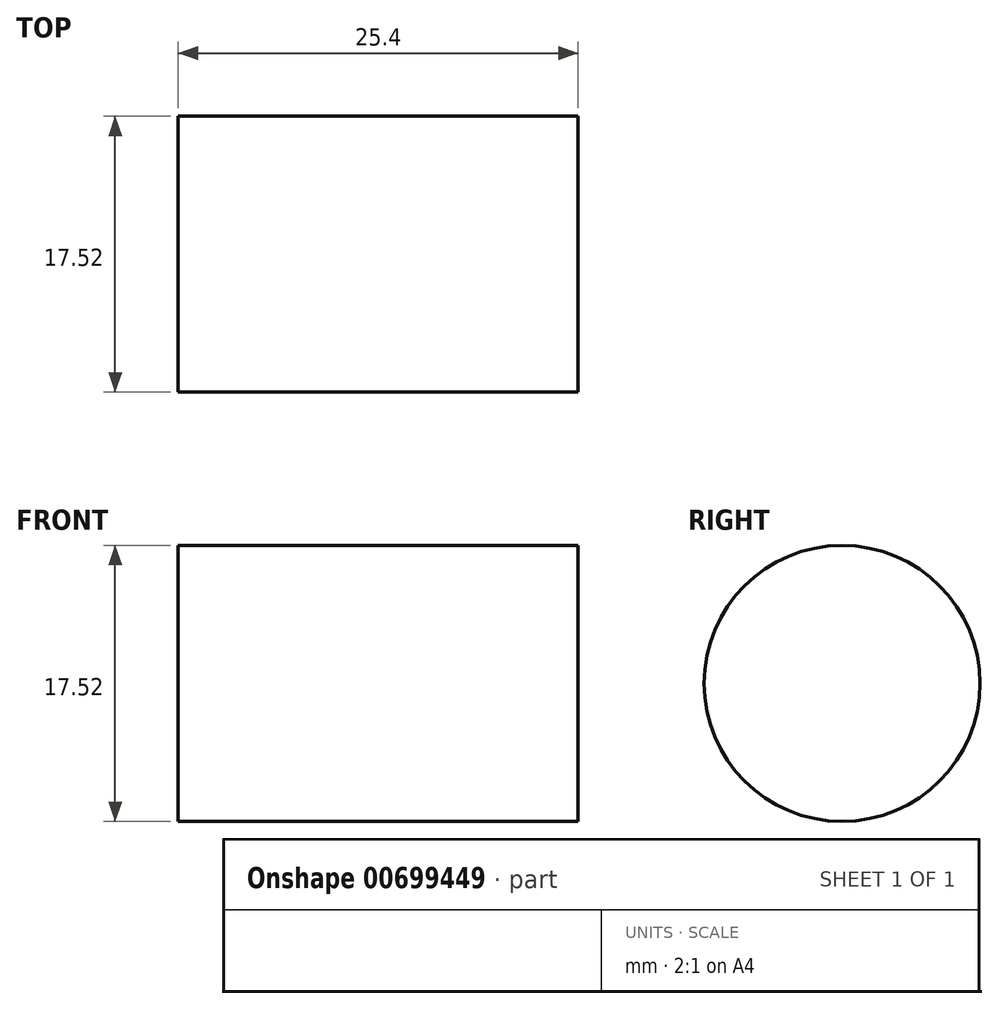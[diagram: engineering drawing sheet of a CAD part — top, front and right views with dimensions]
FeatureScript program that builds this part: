
annotation { "Feature Type Name" : "Feature", "Feature Type Description" : "" }
export const myFeature = defineFeature(function(context is Context, id is Id, definition is map)
    precondition{}
    {
        {
            var Q0;
            Q0=qCreatedBy(makeId("Right.planeOp"),FACE);
            var sketch = newSketch(context, id + "F0", { "sketchPlane" : qUnion([Q0])});
            skCircle(sketch, "E0", {"center": v(0, 0) * mm, "radius": 8.76 * mm});
            skSolve(sketch);
        }
        {
            var Q0;
            Q0=makeQuery(id+"F0.imprint","IMPRINT",FACE,{"disambiguationData":[TD([[makeQuery(id+"F0.imprint","IMPRINT",EDGE,{"derivedFrom":sQuery(id+"F0.wireOp",EDGE,"E0")}),1.0]])]});
            extrude(context, id + "F1", {"entities" : qUnion([Q0]), "oppositeDirection" : true, "depth" : 25.4 * mm, "offsetDistance" : 25.4 * mm});
        }
    });
